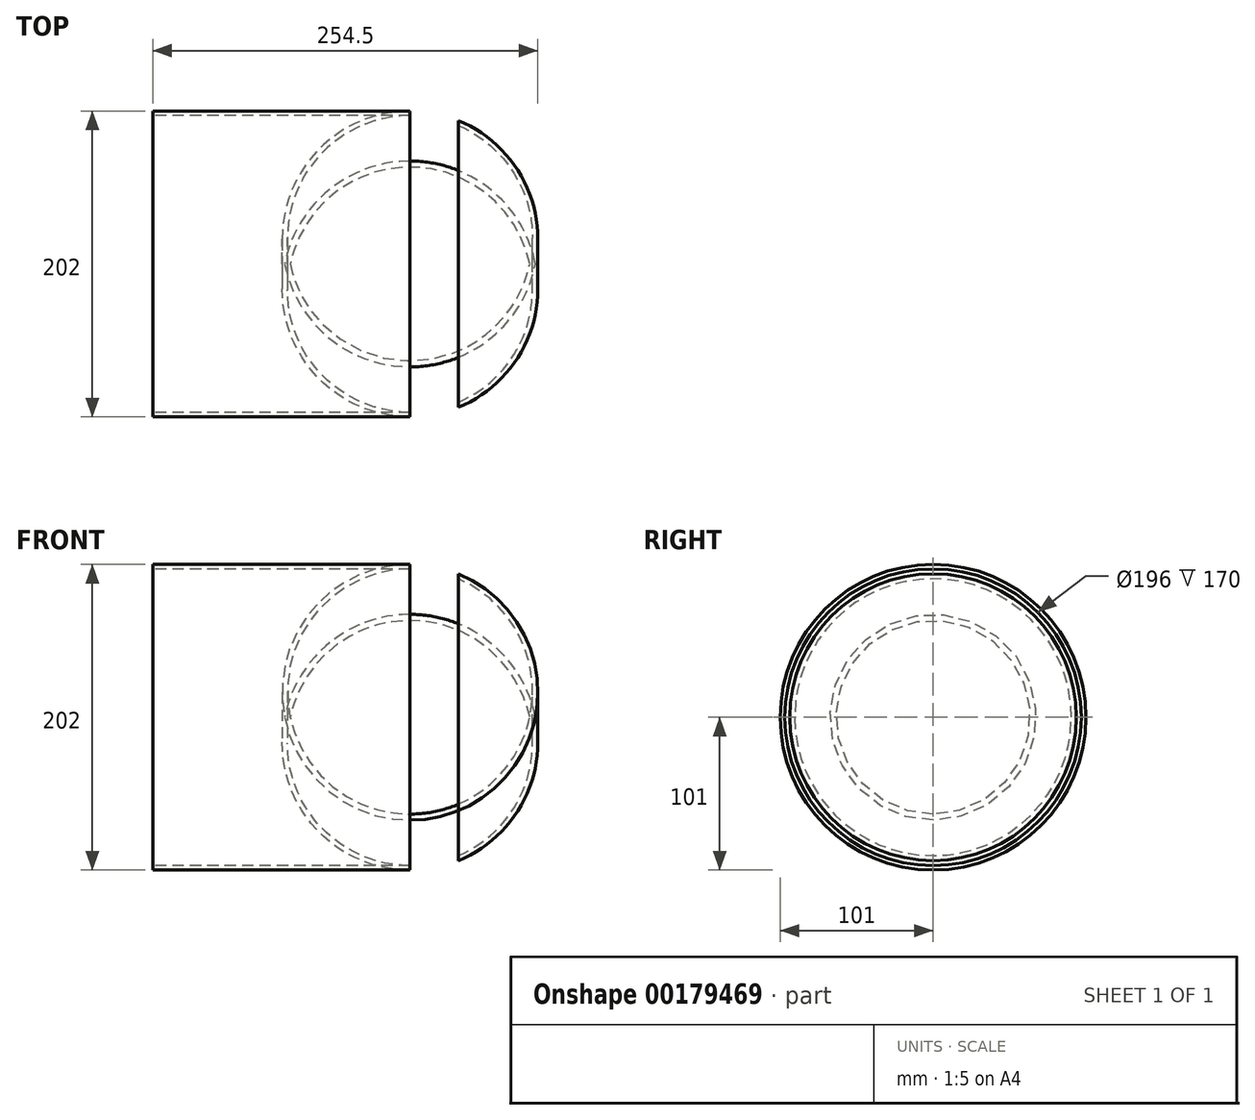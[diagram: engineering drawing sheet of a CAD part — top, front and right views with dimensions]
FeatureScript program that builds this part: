
annotation { "Feature Type Name" : "Feature", "Feature Type Description" : "" }
export const myFeature = defineFeature(function(context is Context, id is Id, definition is map)
    precondition{}
    {
        {
            var Q0;
            Q0=qCreatedBy(makeId("Front.planeOp"),FACE);
            var sketch = newSketch(context, id + "F0", { "sketchPlane" : qUnion([Q0])});
            skLineSegment(sketch, "E0", {"start": v(0, 0) * mm, "end": v(170, 0) * mm});
            skLineSegment(sketch, "E1", {"start": v(0, -3) * mm, "end": v(170, -3) * mm});
            skLineSegment(sketch, "E2", {"start": v(0, 0) * mm, "end": v(0, -3) * mm});
            skArc(sketch, "E3", {"start": v(170, -3) * mm, "mid": v(186.3, -1.41) * mm, "end": v(202, 3.3) * mm});
            skArc(sketch, "E4", {"start": v(170, 0) * mm, "mid": v(186.34, 1.66) * mm, "end": v(202, 6.59) * mm});
            skLineSegment(sketch, "E5", {"start": v(0, -3) * mm, "end": v(202, -3) * mm, "construction": true});
            skLineSegment(sketch, "E6", {"start": v(202, -24.86) * mm, "end": v(202, -3) * mm, "construction": true});
            skLineSegment(sketch, "E7", {"start": v(202, 6.59) * mm, "end": v(202, 3.3) * mm});
            skLineSegment(sketch, "E8", {"start": v(-168.44, 98) * mm, "end": v(309.65, 98) * mm, "construction": true});
            skSolve(sketch);
        }
        {
            var Q0;
            Q0=makeQuery(id+"F0.imprint","IMPRINT",FACE,{"disambiguationData":[TD([[makeQuery(id+"F0.imprint","IMPRINT",EDGE,{"derivedFrom":sQuery(id+"F0.wireOp",EDGE,"E0")}),-1.0]])]});
            var Q1;
            Q1=sQuery(id+"F0.wireOp",EDGE,"E8");
            revolve(context, id + "F1", {"entities" : qUnion([Q0]), "axis" : qUnion([Q1]), "revolveType" : RevolveType.FULL});
        }
    });
